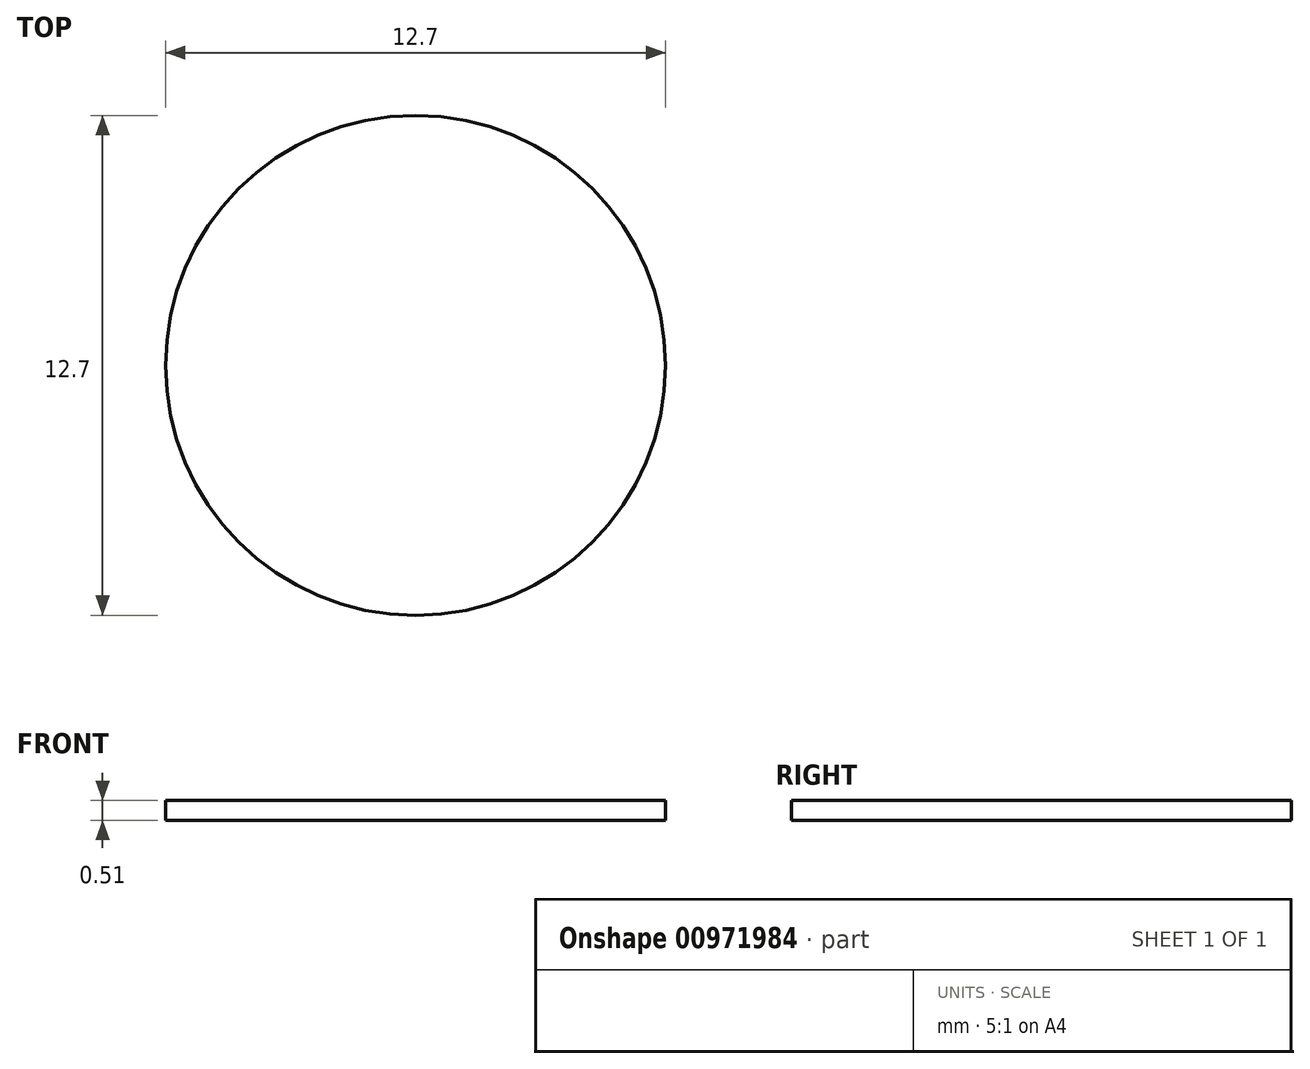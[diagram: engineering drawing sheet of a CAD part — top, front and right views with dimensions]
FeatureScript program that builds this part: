
annotation { "Feature Type Name" : "Feature", "Feature Type Description" : "" }
export const myFeature = defineFeature(function(context is Context, id is Id, definition is map)
    precondition{}
    {
        {
            var Q0;
            Q0=qCreatedBy(makeId("Top.planeOp"),FACE);
            var sketch = newSketch(context, id + "F0", { "sketchPlane" : qUnion([Q0])});
            skCircle(sketch, "E0", {"center": v(0, 0) * mm, "radius": 6.35 * mm});
            skSolve(sketch);
        }
        {
            var Q0;
            Q0=makeQuery(id+"F0.imprint","IMPRINT",FACE,{"disambiguationData":[TD([[makeQuery(id+"F0.imprint","IMPRINT",EDGE,{"derivedFrom":sQuery(id+"F0.wireOp",EDGE,"E0")}),1.0]])]});
            extrude(context, id + "F1", {"entities" : qUnion([Q0]), "depth" : 0.5 * mm, "offsetDistance" : 25.4 * mm});
        }
    });
